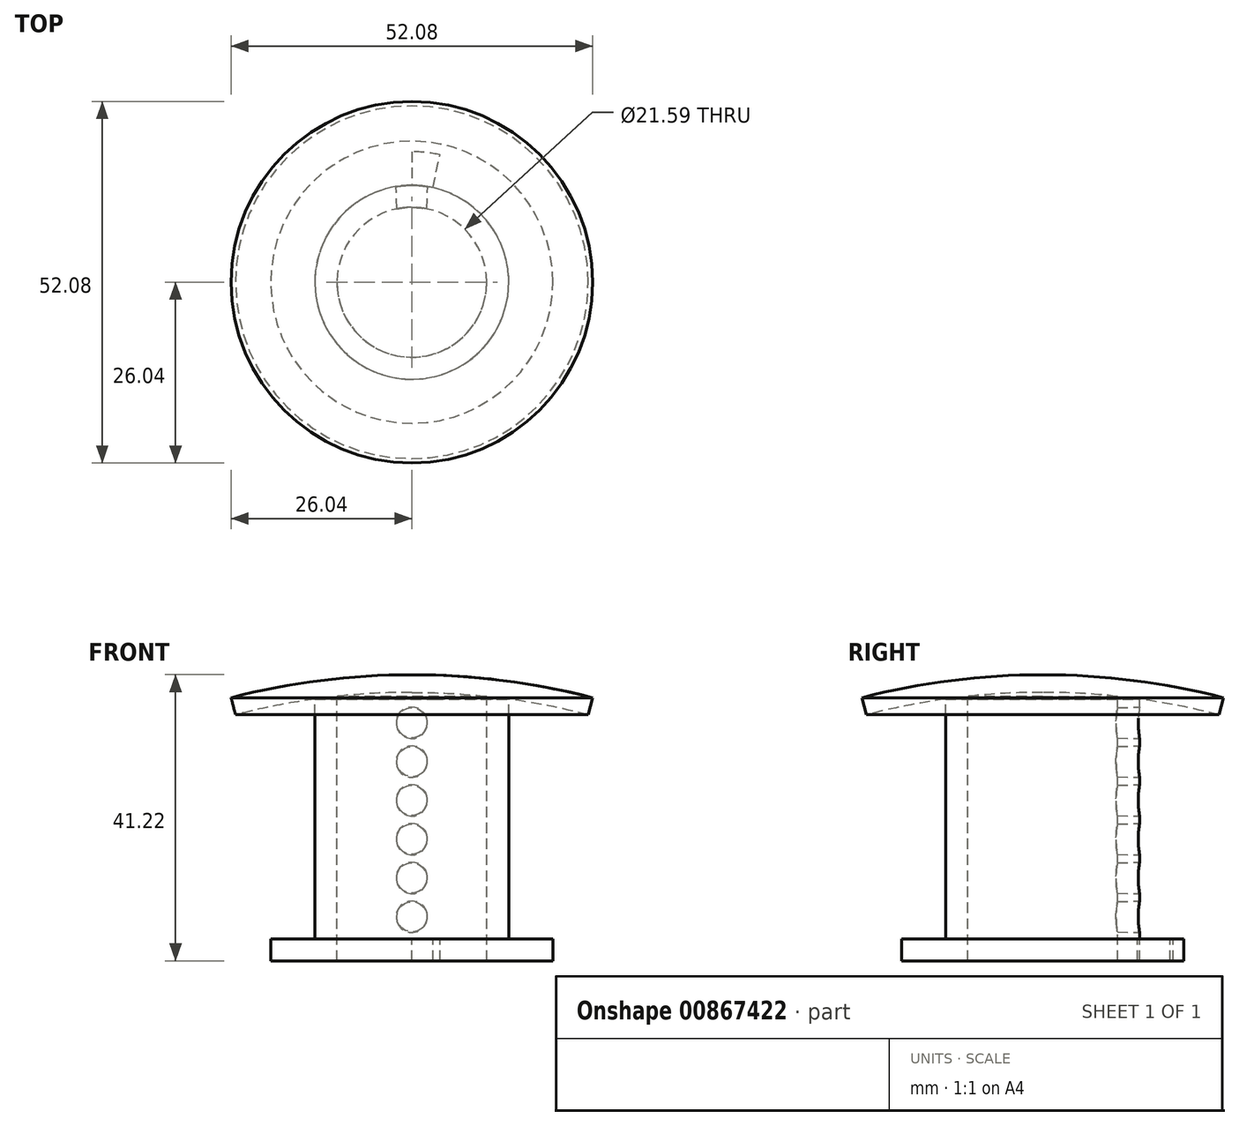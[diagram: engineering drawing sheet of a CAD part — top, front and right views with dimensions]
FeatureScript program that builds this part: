
annotation { "Feature Type Name" : "Feature", "Feature Type Description" : "" }
export const myFeature = defineFeature(function(context is Context, id is Id, definition is map)
    precondition{}
    {
        {
            var Q0;
            Q0=qCreatedBy(makeId("Front.planeOp"),FACE);
            var sketch = newSketch(context, id + "F0", { "sketchPlane" : qUnion([Q0])});
            skLineSegment(sketch, "E0", {"start": v(-10.8, 0) * mm, "end": v(-20.32, 0) * mm});
            skLineSegment(sketch, "E1", {"start": v(-20.32, 0) * mm, "end": v(-20.32, 3.17) * mm});
            skLineSegment(sketch, "E2", {"start": v(-20.32, 3.17) * mm, "end": v(-13.97, 3.17) * mm});
            skLineSegment(sketch, "E3", {"start": v(-13.97, 3.17) * mm, "end": v(-13.97, 38.1) * mm});
            skLineSegment(sketch, "E4", {"start": v(-13.97, 38.1) * mm, "end": v(-10.8, 38.1) * mm});
            skLineSegment(sketch, "E5", {"start": v(-10.8, 38.1) * mm, "end": v(-10.8, 3.18) * mm});
            skLineSegment(sketch, "E6", {"start": v(-10.8, 3.17) * mm, "end": v(-10.8, 3.17) * mm});
            skLineSegment(sketch, "E7", {"start": v(0, 3.18) * mm, "end": v(0, 0) * mm, "construction": true});
            skLineSegment(sketch, "E8", {"start": v(-10.8, 3.17) * mm, "end": v(-10.8, 0) * mm});
            skSolve(sketch);
        }
        {
            var Q0;
            Q0=qSketchRegion(id+"F0",true);
            var Q1;
            Q1=sQuery(id+"F0.wireOp",EDGE,"E7");
            revolve(context, id + "F1", {"surfaceOperationType" : NewSurfaceOperationType.NEW, "entities" : qUnion([Q0]), "axis" : qUnion([Q1]), "revolveType" : RevolveType.FULL});
        }
        {
            var Q0;
            Q0=makeQuery(id+"F1.opRevolve","SWEPT_FACE",FACE,{"disambiguationData":[OSD([sQuery(id+"F0.wireOp",EDGE,"E2")])]});
            var sketch = newSketch(context, id + "F2", { "sketchPlane" : qUnion([Q0])});
            skArc(sketch, "E9", {"start": v(4.07, 18.35) * mm, "mid": v(2.05, 18.68) * mm, "end": v(0, 18.8) * mm, "construction": true});
            skLineSegment(sketch, "E10", {"start": v(0, 18.8) * mm, "end": v(0, 13.97) * mm});
            skLineSegment(sketch, "E11", {"start": v(3.02, 13.64) * mm, "end": v(4.07, 18.35) * mm});
            skArc(sketch, "E12", {"start": v(0, 18.8) * mm, "mid": v(2.05, 18.68) * mm, "end": v(4.07, 18.35) * mm});
            skArc(sketch, "E13", {"start": v(0, 13.97) * mm, "mid": v(1.52, 13.89) * mm, "end": v(3.02, 13.64) * mm});
            skSolve(sketch);
        }
        {
            var Q0;
            Q0=qCreatedBy(makeId("Front.planeOp"),FACE);
            var sketch = newSketch(context, id + "F3", { "sketchPlane" : qUnion([Q0])});
            skLineSegment(sketch, "E14", {"start": v(0, 47.46) * mm, "end": v(0, 0) * mm, "construction": true});
            skSolve(sketch);
        }
        {
            var Q0;
            Q0=makeQuery(id+"F2.imprint","IMPRINT",FACE,{"disambiguationData":[TD([[makeQuery(id+"F2.imprint","IMPRINT",EDGE,{"derivedFrom":sQuery(id+"F2.wireOp",EDGE,"E10")}),1.0]])]});
            extrude(context, id + "F4", {"entities" : qUnion([Q0]), "operationType" : NewBodyOperationType.REMOVE, "endBound" : BoundingType.THROUGH_ALL, "oppositeDirection" : true, "depth" : 25.4 * mm, "offsetDistance" : 25.4 * mm});
        }
        {
            var Q0;
            Q0=qCreatedBy(makeId("Front.planeOp"),FACE);
            var sketch = newSketch(context, id + "F5", { "sketchPlane" : qUnion([Q0])});
            skCircle(sketch, "E15", {"center": v(0, 6.35) * mm, "radius": 1.9 * mm});
            skCircle(sketch, "E16.0.1.0", {"center": v(0, 11.94) * mm, "radius": 1.9 * mm});
            skCircle(sketch, "E16.0.2.0", {"center": v(0, 17.53) * mm, "radius": 1.9 * mm});
            skCircle(sketch, "E16.0.3.0", {"center": v(0, 23.11) * mm, "radius": 1.9 * mm});
            skCircle(sketch, "E16.0.4.0", {"center": v(0, 28.7) * mm, "radius": 1.9 * mm});
            skCircle(sketch, "E16.0.5.0", {"center": v(0, 34.3) * mm, "radius": 1.9 * mm});
            skLineSegment(sketch, "E16.direction1", {"start": v(0, 6.35) * mm, "end": v(25.4, 6.35) * mm, "construction": true});
            skLineSegment(sketch, "E16.direction2", {"start": v(0, 6.35) * mm, "end": v(0, 11.94) * mm, "construction": true});
            skSolve(sketch);
        }
        {
            var Q0;
            Q0=makeQuery(id+"F5.imprint","IMPRINT",FACE,{"disambiguationData":[TD([[makeQuery(id+"F5.imprint","IMPRINT",EDGE,{"derivedFrom":sQuery(id+"F5.wireOp",EDGE,"E16.0.5.0")}),1.0]])]});
            var Q1;
            Q1=makeQuery(id+"F5.imprint","IMPRINT",FACE,{"disambiguationData":[TD([[makeQuery(id+"F5.imprint","IMPRINT",EDGE,{"derivedFrom":sQuery(id+"F5.wireOp",EDGE,"E16.0.4.0")}),1.0]])]});
            var Q2;
            Q2=makeQuery(id+"F5.imprint","IMPRINT",FACE,{"disambiguationData":[TD([[makeQuery(id+"F5.imprint","IMPRINT",EDGE,{"derivedFrom":sQuery(id+"F5.wireOp",EDGE,"E16.0.3.0")}),1.0]])]});
            var Q3;
            Q3=makeQuery(id+"F5.imprint","IMPRINT",FACE,{"disambiguationData":[TD([[makeQuery(id+"F5.imprint","IMPRINT",EDGE,{"derivedFrom":sQuery(id+"F5.wireOp",EDGE,"E15")}),1.0]])]});
            var Q4;
            Q4=makeQuery(id+"F5.imprint","IMPRINT",FACE,{"disambiguationData":[TD([[makeQuery(id+"F5.imprint","IMPRINT",EDGE,{"derivedFrom":sQuery(id+"F5.wireOp",EDGE,"E16.0.1.0")}),1.0]])]});
            var Q5;
            Q5=makeQuery(id+"F5.imprint","IMPRINT",FACE,{"disambiguationData":[TD([[makeQuery(id+"F5.imprint","IMPRINT",EDGE,{"derivedFrom":sQuery(id+"F5.wireOp",EDGE,"E16.0.2.0")}),1.0]])]});
            extrude(context, id + "F6", {"entities" : qUnion([Q0, Q1, Q2, Q3, Q4, Q5]), "operationType" : NewBodyOperationType.REMOVE, "endBound" : BoundingType.THROUGH_ALL, "oppositeDirection" : true, "depth" : 25.4 * mm, "offsetDistance" : 25.4 * mm, "hasDraft" : true, "draftAngle" : 1.5 * degree});
        }
        {
            var Q0;
            Q0=qCreatedBy(makeId("Front.planeOp"),FACE);
            var sketch = newSketch(context, id + "F7", { "sketchPlane" : qUnion([Q0])});
            skArc(sketch, "E17", {"start": v(-25.4, 35.45) * mm, "mid": v(-12.8, 37.87) * mm, "end": v(0, 38.68) * mm});
            skLineSegment(sketch, "E18.0", {"start": v(-10.8, 38.1) * mm, "end": v(10.8, 38.1) * mm, "construction": true});
            skLineSegment(sketch, "E19.0", {"start": v(-13.97, 38.1) * mm, "end": v(13.97, 38.1) * mm, "construction": true});
            skLineSegment(sketch, "E20", {"start": v(0, -62.92) * mm, "end": v(0, 38.68) * mm, "construction": true});
            skPoint(sketch, "E21.orphan", {"position": v(25.4, 35.45) * mm});
            skArc(sketch, "E22.0", {"start": v(-26.04, 37.9) * mm, "mid": v(-13.12, 40.39) * mm, "end": v(0, 41.22) * mm});
            skLineSegment(sketch, "E23", {"start": v(0, 41.22) * mm, "end": v(0, 38.68) * mm});
            skLineSegment(sketch, "E24", {"start": v(-26.04, 37.9) * mm, "end": v(-25.4, 35.45) * mm});
            skSolve(sketch);
        }
        {
            var Q0;
            Q0 = qSketchRegion(id + "F7", true);
            var Q1;
            Q1=sQuery(id+"F7.wireOp",EDGE,"E20");
            revolve(context, id + "F8", {"operationType" : NewBodyOperationType.ADD, "surfaceOperationType" : NewSurfaceOperationType.NEW, "entities" : qUnion([Q0]), "axis" : qUnion([Q1]), "revolveType" : RevolveType.FULL});
        }
    });
